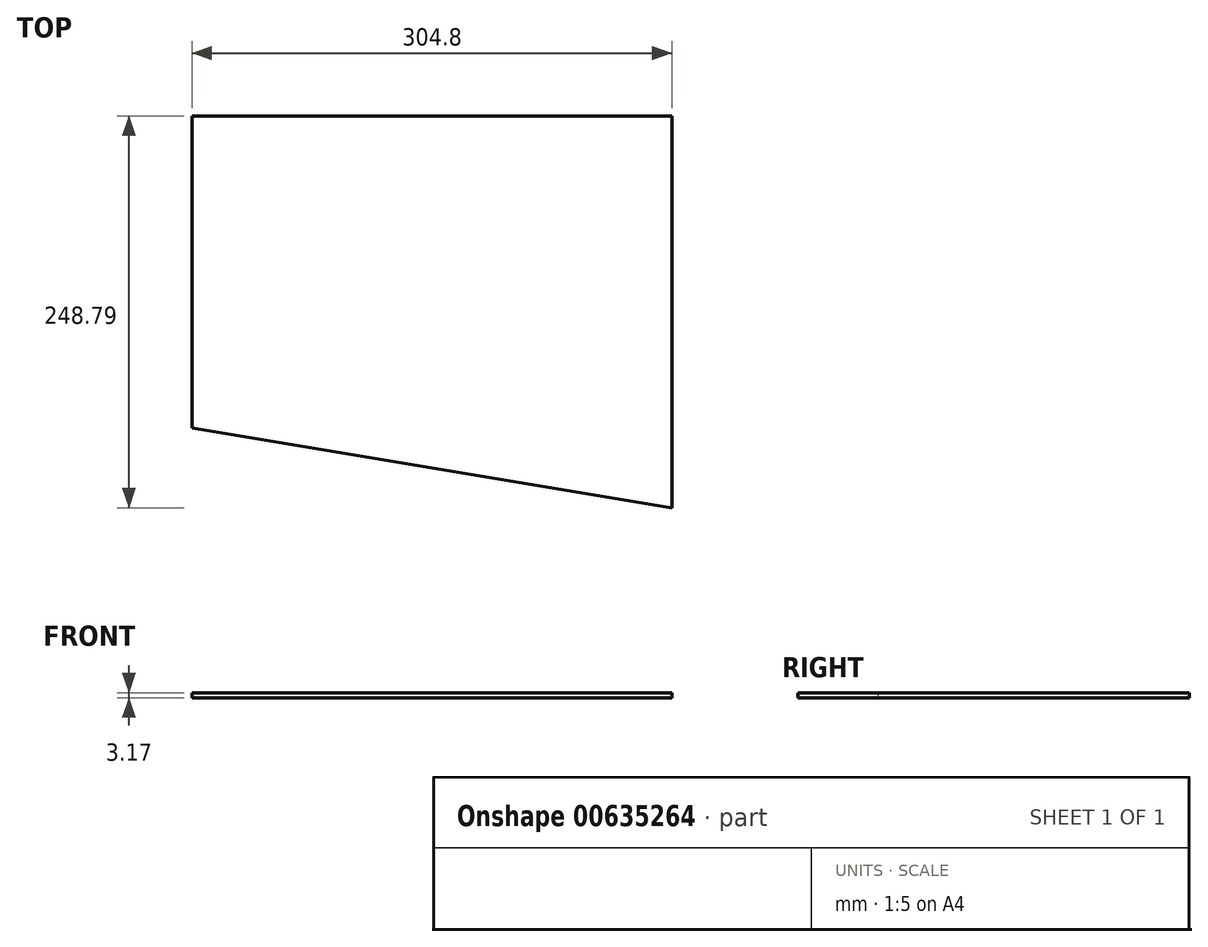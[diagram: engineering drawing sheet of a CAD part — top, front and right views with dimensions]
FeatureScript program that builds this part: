
annotation { "Feature Type Name" : "Feature", "Feature Type Description" : "" }
export const myFeature = defineFeature(function(context is Context, id is Id, definition is map)
    precondition{}
    {
        {
            var Q0;
            Q0=qCreatedBy(makeId("Top.planeOp"),FACE);
            var sketch = newSketch(context, id + "F0", { "sketchPlane" : qUnion([Q0])});
            skLineSegment(sketch, "E0.bottom", {"start": v(0, 0) * mm, "end": v(-304.8, 0) * mm});
            skLineSegment(sketch, "E0.top", {"start": v(0, 248.8) * mm, "end": v(-304.8, 248.8) * mm});
            skLineSegment(sketch, "E0.left", {"start": v(0, 0) * mm, "end": v(0, 248.8) * mm});
            skLineSegment(sketch, "E0.right", {"start": v(-304.8, 50.8) * mm, "end": v(-304.8, 248.8) * mm});
            skLineSegment(sketch, "E1", {"start": v(0, 0) * mm, "end": v(-304.8, 50.8) * mm});
            skSolve(sketch);
        }
        {
            var Q0;
            Q0 = qSketchRegion(id + "F0", true);
            extrude(context, id + "F1", {"entities" : qUnion([Q0]), "depth" : 3.17 * mm, "offsetDistance" : 25.4 * mm});
        }
    });
